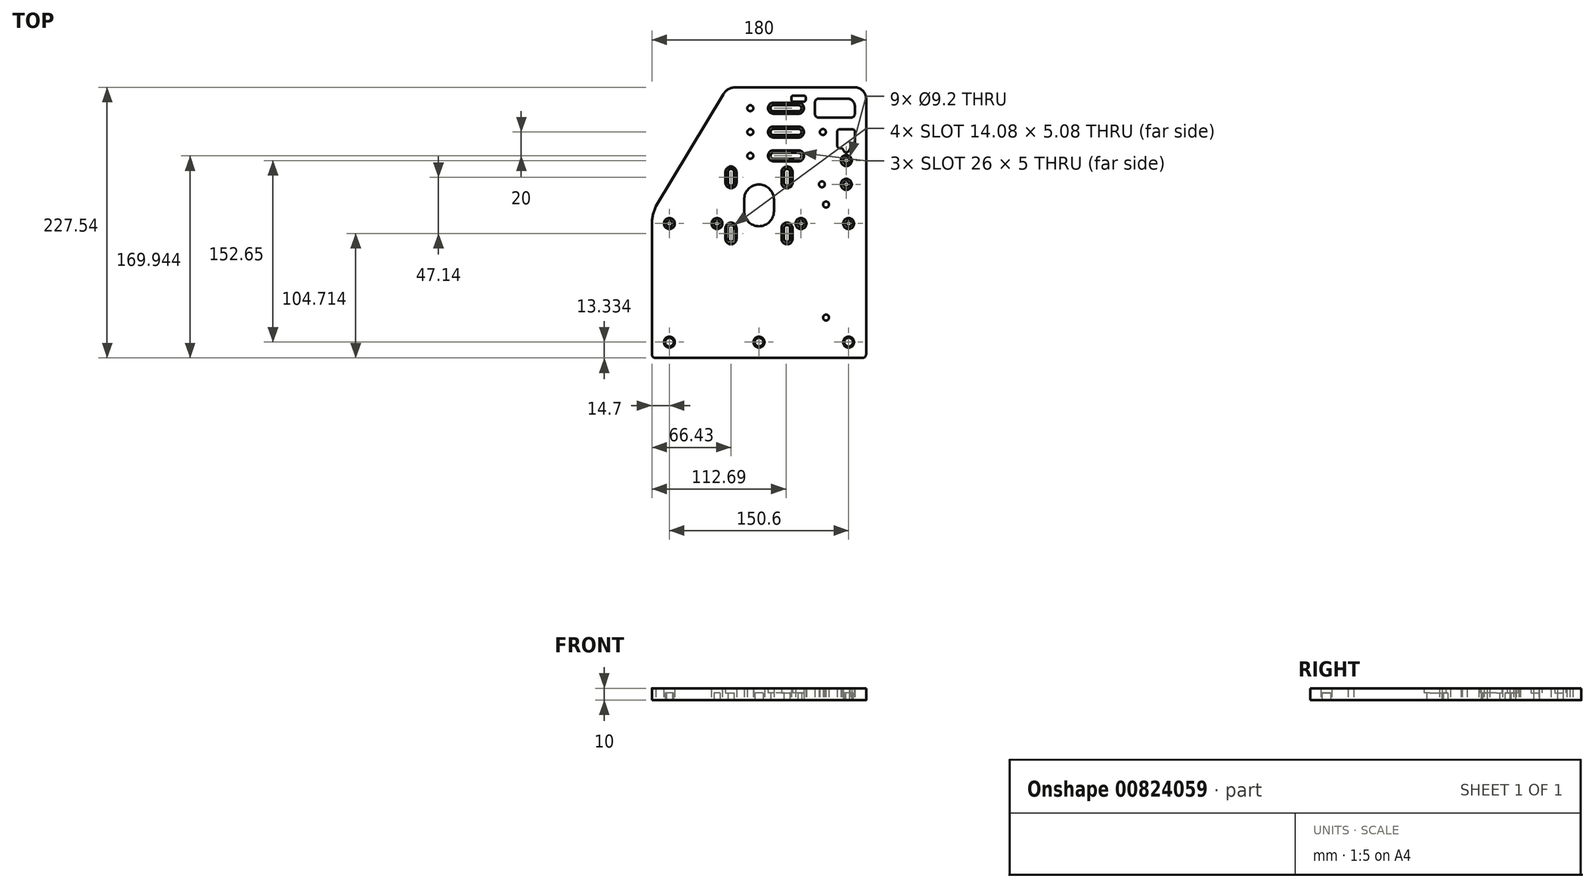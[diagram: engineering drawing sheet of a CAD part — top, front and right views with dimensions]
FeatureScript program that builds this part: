
annotation { "Feature Type Name" : "Feature", "Feature Type Description" : "" }
export const myFeature = defineFeature(function(context is Context, id is Id, definition is map)
    precondition{}
    {
        {
            var Q0;
            Q0=qCreatedBy(makeId("Top.planeOp"),FACE);
            var sketch = newSketch(context, id + "F0", { "sketchPlane" : qUnion([Q0])});
            skLineSegment(sketch, "E0", {"start": v(-86.67, -113.77) * mm, "end": v(86.64, -113.77) * mm});
            skLineSegment(sketch, "E1", {"start": v(-90, -1.46) * mm, "end": v(-90, -110.4) * mm});
            skLineSegment(sketch, "E2", {"start": v(-30.03, 107.94) * mm, "end": v(-86.68, 13.65) * mm});
            skLineSegment(sketch, "E3", {"start": v(-26.11, -13.56) * mm, "end": v(-26.11, -4.56) * mm});
            skLineSegment(sketch, "E4", {"start": v(-26.11, 33.58) * mm, "end": v(-26.11, 42.58) * mm});
            skLineSegment(sketch, "E5", {"start": v(-21.03, 42.58) * mm, "end": v(-21.03, 33.58) * mm});
            skLineSegment(sketch, "E6", {"start": v(-21.03, -4.56) * mm, "end": v(-21.03, -13.56) * mm});
            skLineSegment(sketch, "E7", {"start": v(-12.5, 9.51) * mm, "end": v(-12.5, 19.51) * mm});
            skLineSegment(sketch, "E8", {"start": v(12.5, 19.51) * mm, "end": v(12.5, 9.51) * mm});
            skLineSegment(sketch, "E9", {"start": v(21.03, -13.56) * mm, "end": v(21.03, -4.56) * mm});
            skLineSegment(sketch, "E10", {"start": v(21.03, 33.58) * mm, "end": v(21.03, 42.58) * mm});
            skLineSegment(sketch, "E11", {"start": v(26.1, 42.58) * mm, "end": v(26.1, 33.58) * mm});
            skLineSegment(sketch, "E12", {"start": v(26.1, -4.56) * mm, "end": v(26.1, -13.56) * mm});
            skLineSegment(sketch, "E13", {"start": v(27.19, 103.2) * mm, "end": v(27.19, 105.32) * mm});
            skLineSegment(sketch, "E14", {"start": v(76.37, 62.2) * mm, "end": v(75.8, 61.48) * mm});
            skLineSegment(sketch, "E15", {"start": v(39.19, 105.32) * mm, "end": v(39.19, 103.2) * mm});
            skLineSegment(sketch, "E16", {"start": v(47, 91.4) * mm, "end": v(47, 101.1) * mm});
            skLineSegment(sketch, "E17", {"start": v(33.19, 53.67) * mm, "end": v(12.19, 53.67) * mm});
            skLineSegment(sketch, "E18", {"start": v(12.19, 58.67) * mm, "end": v(33.19, 58.67) * mm});
            skLineSegment(sketch, "E19", {"start": v(65.8, 64.35) * mm, "end": v(65.8, 76.68) * mm});
            skLineSegment(sketch, "E20", {"start": v(78.84, 62.2) * mm, "end": v(76.37, 62.2) * mm});
            skLineSegment(sketch, "E21", {"start": v(69.93, 62.7) * mm, "end": v(67.46, 62.7) * mm});
            skLineSegment(sketch, "E22", {"start": v(33.19, 73.67) * mm, "end": v(12.19, 73.67) * mm});
            skLineSegment(sketch, "E23", {"start": v(67.46, 78.34) * mm, "end": v(78.84, 78.34) * mm});
            skLineSegment(sketch, "E24", {"start": v(80.5, 97.88) * mm, "end": v(80.5, 91.4) * mm});
            skLineSegment(sketch, "E25", {"start": v(80.5, 76.68) * mm, "end": v(80.5, 63.85) * mm});
            skLineSegment(sketch, "E26", {"start": v(12.19, 78.67) * mm, "end": v(33.19, 78.67) * mm});
            skLineSegment(sketch, "E27", {"start": v(77.36, 88.26) * mm, "end": v(50.14, 88.26) * mm});
            skLineSegment(sketch, "E28", {"start": v(90, -110.4) * mm, "end": v(90, 104.05) * mm});
            skLineSegment(sketch, "E29", {"start": v(33.19, 93.67) * mm, "end": v(12.19, 93.67) * mm});
            skLineSegment(sketch, "E30", {"start": v(70.9, 61.48) * mm, "end": v(69.93, 62.7) * mm});
            skLineSegment(sketch, "E31", {"start": v(12.19, 98.67) * mm, "end": v(33.19, 98.67) * mm});
            skLineSegment(sketch, "E32", {"start": v(37.75, 101.76) * mm, "end": v(28.63, 101.76) * mm});
            skLineSegment(sketch, "E33", {"start": v(50.14, 104.23) * mm, "end": v(74.15, 104.23) * mm});
            skLineSegment(sketch, "E34", {"start": v(28.63, 106.76) * mm, "end": v(37.75, 106.76) * mm});
            skLineSegment(sketch, "E35", {"start": v(80.33, 113.73) * mm, "end": v(-18.85, 113.73) * mm});
            skCircle(sketch, "E36", {"center": v(-75.3, -100.44) * mm, "radius": 3.6 * mm});
            skArc(sketch, "E37", {"start": v(-90, -110.4) * mm, "mid": v(-89.03, -112.77) * mm, "end": v(-86.67, -113.77) * mm});
            skArc(sketch, "E38", {"start": v(-26.11, -13.56) * mm, "mid": v(-23.57, -16.1) * mm, "end": v(-21.03, -13.56) * mm});
            skArc(sketch, "E39", {"start": v(-21.03, -4.56) * mm, "mid": v(-23.57, -2.02) * mm, "end": v(-26.11, -4.56) * mm});
            skArc(sketch, "E40", {"start": v(-86.68, 13.65) * mm, "mid": v(-89.16, 6.28) * mm, "end": v(-90, -1.46) * mm});
            skArc(sketch, "E41", {"start": v(-18.85, 113.73) * mm, "mid": v(-25.26, 112.42) * mm, "end": v(-30.03, 107.94) * mm});
            skArc(sketch, "E42", {"start": v(-21.03, 42.58) * mm, "mid": v(-23.57, 45.12) * mm, "end": v(-26.11, 42.58) * mm});
            skArc(sketch, "E43", {"start": v(-26.11, 33.58) * mm, "mid": v(-23.57, 31.04) * mm, "end": v(-21.03, 33.58) * mm});
            skCircle(sketch, "E44", {"center": v(-7.31, 96.17) * mm, "radius": 2.5 * mm});
            skCircle(sketch, "E45", {"center": v(-7.31, 76.17) * mm, "radius": 2.5 * mm});
            skCircle(sketch, "E46", {"center": v(-7.31, 56.17) * mm, "radius": 2.5 * mm});
            skCircle(sketch, "E47", {"center": v(-35.3, -0.74) * mm, "radius": 2.5 * mm});
            skCircle(sketch, "E48", {"center": v(-75.3, -0.74) * mm, "radius": 2.5 * mm});
            skCircle(sketch, "E49", {"center": v(75.3, -100.44) * mm, "radius": 3.6 * mm});
            skCircle(sketch, "E50", {"center": v(0, -100.44) * mm, "radius": 3.6 * mm});
            skArc(sketch, "E51", {"start": v(86.64, -113.77) * mm, "mid": v(89.02, -112.78) * mm, "end": v(90, -110.4) * mm});
            skArc(sketch, "E52", {"start": v(21.03, -13.56) * mm, "mid": v(23.57, -16.1) * mm, "end": v(26.1, -13.56) * mm});
            skArc(sketch, "E53", {"start": v(26.1, -4.56) * mm, "mid": v(23.57, -2.02) * mm, "end": v(21.03, -4.56) * mm});
            skCircle(sketch, "E54", {"center": v(56.34, -79.74) * mm, "radius": 2.5 * mm});
            skArc(sketch, "E55", {"start": v(-12.5, 9.51) * mm, "mid": v(0, -2.99) * mm, "end": v(12.5, 9.51) * mm});
            skArc(sketch, "E56", {"start": v(12.5, 19.51) * mm, "mid": v(0, 32.01) * mm, "end": v(-12.5, 19.51) * mm});
            skArc(sketch, "E57", {"start": v(90, 104.05) * mm, "mid": v(87.17, 110.9) * mm, "end": v(80.33, 113.73) * mm});
            skArc(sketch, "E58", {"start": v(80.5, 97.88) * mm, "mid": v(78.64, 102.37) * mm, "end": v(74.15, 104.23) * mm});
            skArc(sketch, "E59", {"start": v(77.36, 88.26) * mm, "mid": v(79.58, 89.18) * mm, "end": v(80.5, 91.4) * mm});
            skArc(sketch, "E60", {"start": v(47, 91.4) * mm, "mid": v(47.92, 89.18) * mm, "end": v(50.14, 88.26) * mm});
            skArc(sketch, "E61", {"start": v(50.14, 104.23) * mm, "mid": v(47.92, 103.31) * mm, "end": v(47, 101.1) * mm});
            skArc(sketch, "E62", {"start": v(21.03, 33.58) * mm, "mid": v(23.57, 31.04) * mm, "end": v(26.1, 33.58) * mm});
            skArc(sketch, "E63", {"start": v(26.1, 42.58) * mm, "mid": v(23.57, 45.12) * mm, "end": v(21.03, 42.58) * mm});
            skArc(sketch, "E64", {"start": v(33.19, 93.67) * mm, "mid": v(35.69, 96.17) * mm, "end": v(33.19, 98.67) * mm});
            skArc(sketch, "E65", {"start": v(12.19, 98.67) * mm, "mid": v(9.69, 96.17) * mm, "end": v(12.19, 93.67) * mm});
            skArc(sketch, "E66", {"start": v(33.19, 73.67) * mm, "mid": v(35.69, 76.17) * mm, "end": v(33.19, 78.67) * mm});
            skArc(sketch, "E67", {"start": v(12.19, 78.67) * mm, "mid": v(9.69, 76.17) * mm, "end": v(12.19, 73.67) * mm});
            skArc(sketch, "E68", {"start": v(33.19, 53.67) * mm, "mid": v(35.69, 56.17) * mm, "end": v(33.19, 58.67) * mm});
            skArc(sketch, "E69", {"start": v(12.19, 58.67) * mm, "mid": v(9.69, 56.17) * mm, "end": v(12.19, 53.67) * mm});
            skCircle(sketch, "E70", {"center": v(53.69, 76.17) * mm, "radius": 2.5 * mm});
            skCircle(sketch, "E71", {"center": v(73.35, 52.21) * mm, "radius": 2.5 * mm});
            skCircle(sketch, "E72", {"center": v(73.35, 32.21) * mm, "radius": 2.5 * mm});
            skCircle(sketch, "E73", {"center": v(52.85, 32.21) * mm, "radius": 2.5 * mm});
            skCircle(sketch, "E74", {"center": v(56.34, 15.26) * mm, "radius": 2.5 * mm});
            skCircle(sketch, "E75", {"center": v(75.3, -0.74) * mm, "radius": 2.5 * mm});
            skCircle(sketch, "E76", {"center": v(35.3, -0.74) * mm, "radius": 2.5 * mm});
            skArc(sketch, "E77", {"start": v(80.5, 76.68) * mm, "mid": v(80.01, 77.86) * mm, "end": v(78.84, 78.34) * mm});
            skArc(sketch, "E78", {"start": v(78.84, 62.2) * mm, "mid": v(80.01, 62.68) * mm, "end": v(80.5, 63.85) * mm});
            skArc(sketch, "E79", {"start": v(65.8, 64.35) * mm, "mid": v(66.29, 63.18) * mm, "end": v(67.46, 62.7) * mm});
            skArc(sketch, "E80", {"start": v(67.46, 78.34) * mm, "mid": v(66.29, 77.86) * mm, "end": v(65.8, 76.68) * mm});
            skArc(sketch, "E81", {"start": v(39.19, 105.32) * mm, "mid": v(38.77, 106.34) * mm, "end": v(37.75, 106.76) * mm});
            skArc(sketch, "E82", {"start": v(37.75, 101.76) * mm, "mid": v(38.77, 102.19) * mm, "end": v(39.19, 103.2) * mm});
            skArc(sketch, "E83", {"start": v(27.19, 103.2) * mm, "mid": v(27.61, 102.19) * mm, "end": v(28.63, 101.76) * mm});
            skArc(sketch, "E84", {"start": v(28.63, 106.76) * mm, "mid": v(27.61, 106.34) * mm, "end": v(27.19, 105.32) * mm});
            skEllipticalArc(sketch, "E85", {});
            skArc(sketch, "E86.0", {"start": v(-28.21, -13.56) * mm, "mid": v(-23.57, -18.2) * mm, "end": v(-18.93, -13.56) * mm});
            skLineSegment(sketch, "E86.1", {"start": v(-28.21, -13.56) * mm, "end": v(-28.21, -4.56) * mm});
            skArc(sketch, "E86.2", {"start": v(-18.93, -4.56) * mm, "mid": v(-23.57, 0.08) * mm, "end": v(-28.21, -4.56) * mm});
            skLineSegment(sketch, "E86.3", {"start": v(-18.93, -4.56) * mm, "end": v(-18.93, -13.56) * mm});
            skArc(sketch, "E87.0", {"start": v(-18.93, 42.58) * mm, "mid": v(-23.57, 47.22) * mm, "end": v(-28.21, 42.58) * mm});
            skLineSegment(sketch, "E87.1", {"start": v(-18.93, 42.58) * mm, "end": v(-18.93, 33.58) * mm});
            skArc(sketch, "E87.2", {"start": v(-28.21, 33.58) * mm, "mid": v(-23.57, 28.94) * mm, "end": v(-18.93, 33.58) * mm});
            skLineSegment(sketch, "E87.3", {"start": v(-28.21, 33.58) * mm, "end": v(-28.21, 42.58) * mm});
            skArc(sketch, "E88.0", {"start": v(18.93, 33.58) * mm, "mid": v(23.57, 28.94) * mm, "end": v(28.2, 33.58) * mm});
            skLineSegment(sketch, "E88.1", {"start": v(18.93, 33.58) * mm, "end": v(18.93, 42.58) * mm});
            skArc(sketch, "E88.2", {"start": v(28.2, 42.58) * mm, "mid": v(23.57, 47.22) * mm, "end": v(18.93, 42.58) * mm});
            skLineSegment(sketch, "E88.3", {"start": v(28.2, 42.58) * mm, "end": v(28.2, 33.58) * mm});
            skArc(sketch, "E89.0", {"start": v(28.2, -4.56) * mm, "mid": v(23.57, 0.08) * mm, "end": v(18.93, -4.56) * mm});
            skLineSegment(sketch, "E89.1", {"start": v(28.2, -4.56) * mm, "end": v(28.2, -13.56) * mm});
            skArc(sketch, "E89.2", {"start": v(18.93, -13.56) * mm, "mid": v(23.57, -18.2) * mm, "end": v(28.2, -13.56) * mm});
            skLineSegment(sketch, "E89.3", {"start": v(18.93, -13.56) * mm, "end": v(18.93, -4.56) * mm});
            skCircle(sketch, "E90.0", {"center": v(-75.3, -100.44) * mm, "radius": 4.6 * mm});
            skCircle(sketch, "E91.0", {"center": v(0, -100.44) * mm, "radius": 4.6 * mm});
            skCircle(sketch, "E92.0", {"center": v(75.3, -100.44) * mm, "radius": 4.6 * mm});
            skCircle(sketch, "E93.0", {"center": v(75.3, -0.74) * mm, "radius": 4.6 * mm});
            skCircle(sketch, "E94.0", {"center": v(35.3, -0.74) * mm, "radius": 4.6 * mm});
            skCircle(sketch, "E95.0", {"center": v(-35.3, -0.74) * mm, "radius": 4.6 * mm});
            skCircle(sketch, "E96.0", {"center": v(-75.3, -0.74) * mm, "radius": 4.6 * mm});
            skArc(sketch, "E97.0", {"start": v(33.19, 91.57) * mm, "mid": v(37.79, 96.17) * mm, "end": v(33.19, 100.77) * mm});
            skLineSegment(sketch, "E97.1", {"start": v(33.19, 91.57) * mm, "end": v(12.19, 91.57) * mm});
            skArc(sketch, "E97.2", {"start": v(12.19, 100.77) * mm, "mid": v(7.59, 96.17) * mm, "end": v(12.19, 91.57) * mm});
            skLineSegment(sketch, "E97.3", {"start": v(12.19, 100.77) * mm, "end": v(33.19, 100.77) * mm});
            skArc(sketch, "E98.0", {"start": v(33.19, 71.57) * mm, "mid": v(37.79, 76.17) * mm, "end": v(33.19, 80.77) * mm});
            skLineSegment(sketch, "E98.1", {"start": v(33.19, 71.57) * mm, "end": v(12.19, 71.57) * mm});
            skArc(sketch, "E98.2", {"start": v(12.19, 80.77) * mm, "mid": v(7.59, 76.17) * mm, "end": v(12.19, 71.57) * mm});
            skLineSegment(sketch, "E98.3", {"start": v(12.19, 80.77) * mm, "end": v(33.19, 80.77) * mm});
            skLineSegment(sketch, "E99.0", {"start": v(12.19, 60.77) * mm, "end": v(33.19, 60.77) * mm});
            skArc(sketch, "E99.1", {"start": v(12.19, 60.77) * mm, "mid": v(7.59, 56.17) * mm, "end": v(12.19, 51.57) * mm});
            skLineSegment(sketch, "E99.2", {"start": v(33.19, 51.57) * mm, "end": v(12.19, 51.57) * mm});
            skArc(sketch, "E99.3", {"start": v(33.19, 51.57) * mm, "mid": v(37.79, 56.17) * mm, "end": v(33.19, 60.77) * mm});
            skCircle(sketch, "E100.0", {"center": v(73.35, 52.21) * mm, "radius": 4.6 * mm});
            skCircle(sketch, "E101.0", {"center": v(73.35, 32.21) * mm, "radius": 4.6 * mm});
            const initialGuessF0  = {"E85": [0.073349997, 0.06148353900000001, 2.452987, 0, 0.002452987, 0.002452987, -3.141593, 0]};
            skSetInitialGuess(sketch, initialGuessF0);
            skSolve(sketch);
        }
        {
            var Q0;
            Q0 = qSketchRegion(id + "F0", true);
            extrude(context, id + "F1", {"entities" : qUnion([Q0]), "depth" : 10 * mm, "offsetDistance" : 25 * mm});
        }
        {
            var Q0;
            Q0=makeQuery(id+"F0.imprint","IMPRINT",FACE,{"disambiguationData":[TD([[makeQuery(id+"F0.imprint","IMPRINT",EDGE,{"derivedFrom":sQuery(id+"F0.wireOp",EDGE,"E36")}),1.0]])]});
            var Q1;
            Q1=makeQuery(id+"F0.imprint","IMPRINT",FACE,{"disambiguationData":[TD([[makeQuery(id+"F0.imprint","IMPRINT",EDGE,{"derivedFrom":sQuery(id+"F0.wireOp",EDGE,"E50")}),1.0]])]});
            var Q2;
            Q2=makeQuery(id+"F0.imprint","IMPRINT",FACE,{"disambiguationData":[TD([[makeQuery(id+"F0.imprint","IMPRINT",EDGE,{"derivedFrom":sQuery(id+"F0.wireOp",EDGE,"E49")}),1.0]])]});
            var Q3;
            Q3=makeQuery(id+"F0.imprint","IMPRINT",FACE,{"disambiguationData":[TD([[makeQuery(id+"F0.imprint","IMPRINT",EDGE,{"derivedFrom":sQuery(id+"F0.wireOp",EDGE,"E75")}),1.0]])]});
            var Q4;
            Q4=makeQuery(id+"F0.imprint","IMPRINT",FACE,{"disambiguationData":[TD([[makeQuery(id+"F0.imprint","IMPRINT",EDGE,{"derivedFrom":sQuery(id+"F0.wireOp",EDGE,"E76")}),1.0]])]});
            var Q5;
            Q5=makeQuery(id+"F0.imprint","IMPRINT",FACE,{"disambiguationData":[TD([[makeQuery(id+"F0.imprint","IMPRINT",EDGE,{"derivedFrom":sQuery(id+"F0.wireOp",EDGE,"E47")}),1.0]])]});
            var Q6;
            Q6=makeQuery(id+"F0.imprint","IMPRINT",FACE,{"disambiguationData":[TD([[makeQuery(id+"F0.imprint","IMPRINT",EDGE,{"derivedFrom":sQuery(id+"F0.wireOp",EDGE,"E3")}),1.0]])]});
            var Q7;
            Q7=makeQuery(id+"F0.imprint","IMPRINT",FACE,{"disambiguationData":[TD([[makeQuery(id+"F0.imprint","IMPRINT",EDGE,{"derivedFrom":sQuery(id+"F0.wireOp",EDGE,"E4")}),1.0]])]});
            var Q8;
            Q8=makeQuery(id+"F0.imprint","IMPRINT",FACE,{"disambiguationData":[TD([[makeQuery(id+"F0.imprint","IMPRINT",EDGE,{"derivedFrom":sQuery(id+"F0.wireOp",EDGE,"E10")}),1.0]])]});
            var Q9;
            Q9=makeQuery(id+"F0.imprint","IMPRINT",FACE,{"disambiguationData":[TD([[makeQuery(id+"F0.imprint","IMPRINT",EDGE,{"derivedFrom":sQuery(id+"F0.wireOp",EDGE,"E9")}),1.0]])]});
            var Q10;
            Q10=makeQuery(id+"F0.imprint","IMPRINT",FACE,{"disambiguationData":[TD([[makeQuery(id+"F0.imprint","IMPRINT",EDGE,{"derivedFrom":sQuery(id+"F0.wireOp",EDGE,"E48")}),1.0]])]});
            var Q11;
            Q11=makeQuery(id+"F0.imprint","IMPRINT",FACE,{"disambiguationData":[TD([[makeQuery(id+"F0.imprint","IMPRINT",EDGE,{"derivedFrom":sQuery(id+"F0.wireOp",EDGE,"E22")}),1.0]])]});
            var Q12;
            Q12=makeQuery(id+"F0.imprint","IMPRINT",FACE,{"disambiguationData":[TD([[makeQuery(id+"F0.imprint","IMPRINT",EDGE,{"derivedFrom":sQuery(id+"F0.wireOp",EDGE,"E29")}),1.0]])]});
            var Q13;
            Q13=makeQuery(id+"F0.imprint","IMPRINT",FACE,{"disambiguationData":[TD([[makeQuery(id+"F0.imprint","IMPRINT",EDGE,{"derivedFrom":sQuery(id+"F0.wireOp",EDGE,"E17")}),1.0]])]});
            var Q14;
            Q14=makeQuery(id+"F0.imprint","IMPRINT",FACE,{"disambiguationData":[TD([[makeQuery(id+"F0.imprint","IMPRINT",EDGE,{"derivedFrom":sQuery(id+"F0.wireOp",EDGE,"E71")}),1.0]])]});
            var Q15;
            Q15=makeQuery(id+"F0.imprint","IMPRINT",FACE,{"disambiguationData":[TD([[makeQuery(id+"F0.imprint","IMPRINT",EDGE,{"derivedFrom":sQuery(id+"F0.wireOp",EDGE,"E72")}),1.0]])]});
            extrude(context, id + "F2", {"entities" : qUnion([Q0, Q1, Q2, Q3, Q4, Q5, Q6, Q7, Q8, Q9, Q10, Q11, Q12, Q13, Q14, Q15]), "operationType" : NewBodyOperationType.ADD, "depth" : 6 * mm, "offsetDistance" : 25 * mm});
        }
    });
